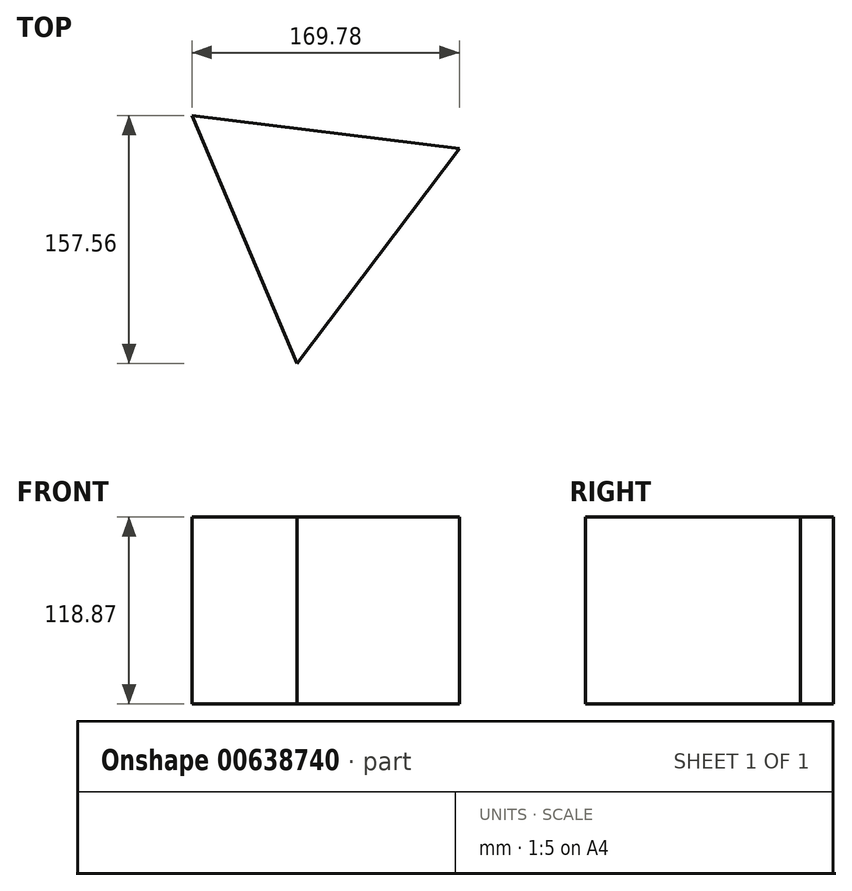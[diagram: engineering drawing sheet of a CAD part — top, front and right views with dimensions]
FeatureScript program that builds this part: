
annotation { "Feature Type Name" : "Feature", "Feature Type Description" : "" }
export const myFeature = defineFeature(function(context is Context, id is Id, definition is map)
    precondition{}
    {
        {
            var Q0;
            Q0=qCreatedBy(makeId("Top.planeOp"),FACE);
            var sketch = newSketch(context, id + "F0", { "sketchPlane" : qUnion([Q0])});
            skCircle(sketch, "E0.cCircle", {"center": v(0, 0) * mm, "radius": 49.39 * mm, "construction": true});
            skLineSegment(sketch, "E0.0", {"start": v(90.97, 38.48) * mm, "end": v(-12.16, -98.02) * mm});
            skLineSegment(sketch, "E0.1", {"start": v(-12.16, -98.02) * mm, "end": v(-78.8, 59.54) * mm});
            skLineSegment(sketch, "E0.2", {"start": v(-78.8, 59.54) * mm, "end": v(90.97, 38.48) * mm});
            skPoint(sketch, "E0.0.midPoint", {"position": v(39.4, -29.77) * mm});
            skSolve(sketch);
        }
        {
            var Q0;
            Q0=makeQuery(id+"F0.imprint","IMPRINT",FACE,{"disambiguationData":[TD([[makeQuery(id+"F0.imprint","IMPRINT",EDGE,{"derivedFrom":sQuery(id+"F0.wireOp",EDGE,"E0.0")}),-1.0]])]});
            extrude(context, id + "F1", {"entities" : qUnion([Q0]), "depth" : 118.87 * mm, "offsetDistance" : 25.4 * mm});
        }
    });
